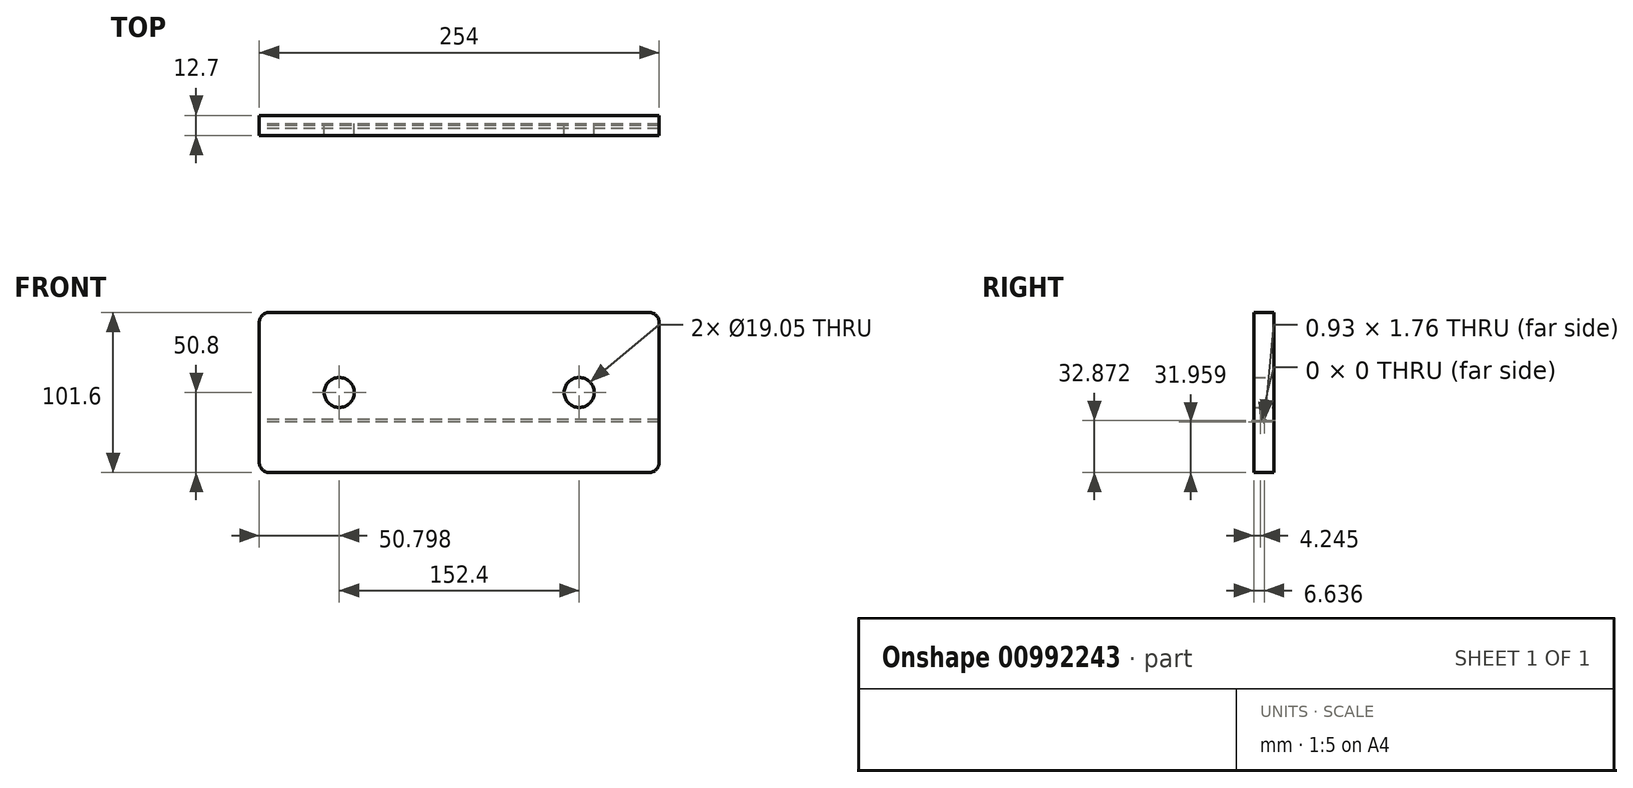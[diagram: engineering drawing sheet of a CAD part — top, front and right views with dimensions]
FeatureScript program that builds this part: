
annotation { "Feature Type Name" : "Feature", "Feature Type Description" : "" }
export const myFeature = defineFeature(function(context is Context, id is Id, definition is map)
    precondition{}
    {
        {
            var Q0;
            Q0=qCreatedBy(makeId("Front.planeOp"),FACE);
            var sketch = newSketch(context, id + "F0", { "sketchPlane" : qUnion([Q0])});
            skLineSegment(sketch, "E0.bottom", {"start": v(16.29, 17.05) * mm, "end": v(270.29, 17.05) * mm});
            skLineSegment(sketch, "E0.top", {"start": v(16.29, 118.65) * mm, "end": v(270.29, 118.65) * mm});
            skLineSegment(sketch, "E0.left", {"start": v(16.29, 17.05) * mm, "end": v(16.29, 118.65) * mm});
            skLineSegment(sketch, "E0.right", {"start": v(270.29, 17.05) * mm, "end": v(270.29, 118.65) * mm});
            skPoint(sketch, "E1", {"position": v(67.09, 67.85) * mm});
            skPoint(sketch, "E2", {"position": v(219.49, 67.85) * mm});
            skCircle(sketch, "E3", {"center": v(67.09, 67.85) * mm, "radius": 9.53 * mm});
            skCircle(sketch, "E4", {"center": v(219.49, 67.85) * mm, "radius": 9.53 * mm});
            skPoint(sketch, "E5.start.orphan", {"position": v(16.29, 67.85) * mm});
            skPoint(sketch, "E6.trimOffspring.end.orphan", {"position": v(270.29, 67.85) * mm});
            skSolve(sketch);
        }
        {
            var Q0;
            Q0 = qSketchRegion(id + "F0", true);
            extrude(context, id + "F1", {"entities" : qUnion([Q0]), "depth" : 12.7 * mm, "offsetDistance" : 25.4 * mm});
        }
        {
            var Q0;
            Q0=makeQuery(id+"F1.opExtrude","SWEPT_EDGE",EDGE,{"disambiguationData":[OSD([sQuery(id+"F0.wireOp",EDGE,"E0.top"),sQuery(id+"F0.wireOp",EDGE,"E0.left")])]});
            var Q1;
            Q1=makeQuery(id+"F1.opExtrude","SWEPT_EDGE",EDGE,{"disambiguationData":[OSD([sQuery(id+"F0.wireOp",EDGE,"E0.bottom"),sQuery(id+"F0.wireOp",EDGE,"E0.left")])]});
            var Q2;
            Q2=makeQuery(id+"F1.opExtrude","SWEPT_EDGE",EDGE,{"disambiguationData":[OSD([sQuery(id+"F0.wireOp",EDGE,"E0.top"),sQuery(id+"F0.wireOp",EDGE,"E0.right")])]});
            var Q3;
            Q3=makeQuery(id+"F1.opExtrude","SWEPT_EDGE",EDGE,{"disambiguationData":[OSD([sQuery(id+"F0.wireOp",EDGE,"E0.bottom"),sQuery(id+"F0.wireOp",EDGE,"E0.right")])]});
            fillet(context, id + "F2", {"entities" : qUnion([Q0, Q1, Q2, Q3]), "radius" : 6.35 * mm, "tangentPropagation" : true, "allowEdgeOverflow" : false});
        }
        {
            var Q0;
            Q0 = qSketchRegion(id + "F0", true);
            extrude(context, id + "F3", {"entities" : qUnion([Q0]), "operationType" : NewBodyOperationType.ADD, "depth" : 12.7 * mm, "offsetDistance" : 25.4 * mm});
        }
        {
            var Q0;
            Q0=makeQuery(id+"F3.opExtrude","SWEPT_EDGE",EDGE,{"disambiguationData":[OSD([sQuery(id+"F0.wireOp",EDGE,"E0.top"),sQuery(id+"F0.wireOp",EDGE,"E0.right")])]});
            var Q1;
            Q1=makeQuery(id+"F3.opExtrude","SWEPT_EDGE",EDGE,{"disambiguationData":[OSD([sQuery(id+"F0.wireOp",EDGE,"E0.top"),sQuery(id+"F0.wireOp",EDGE,"E0.left")])]});
            var Q2;
            Q2=makeQuery(id+"F3.opExtrude","SWEPT_EDGE",EDGE,{"disambiguationData":[OSD([sQuery(id+"F0.wireOp",EDGE,"E0.bottom"),sQuery(id+"F0.wireOp",EDGE,"E0.right")])]});
            var Q3;
            Q3=makeQuery(id+"F3.opExtrude","SWEPT_EDGE",EDGE,{"disambiguationData":[OSD([sQuery(id+"F0.wireOp",EDGE,"E0.bottom"),sQuery(id+"F0.wireOp",EDGE,"E0.left")])]});
            fillet(context, id + "F4", {"entities" : qUnion([Q0, Q1, Q2, Q3]), "radius" : 6.35 * mm, "tangentPropagation" : true, "allowEdgeOverflow" : false});
        }
        {
            var Q0;
            {var subQ0=sQuery(id+"F0.wireOp",EDGE,"E0.left");Q0=makeQuery(id+"F3.boolean.opBoolean","MERGE",FACE,{"derivedFrom":[makeQuery(id+"F1.opExtrude","SWEPT_FACE",FACE,{"disambiguationData":[OSD([subQ0])]}),makeQuery(id+"F3.opExtrude","SWEPT_FACE",FACE,{"disambiguationData":[OSD([subQ0])]})]});}
            var sketch = newSketch(context, id + "F5", { "sketchPlane" : qUnion([Q0])});
            skLineSegment(sketch, "E7.bottom", {"start": v(5.6, 50.8) * mm, "end": v(6.53, 50.8) * mm});
            skLineSegment(sketch, "E7.top", {"start": v(5.6, 49.04) * mm, "end": v(6.53, 49.04) * mm});
            skLineSegment(sketch, "E7.left", {"start": v(5.6, 49.04) * mm, "end": v(5.6, 50.8) * mm});
            skLineSegment(sketch, "E7.right", {"start": v(6.53, 49.04) * mm, "end": v(6.53, 50.8) * mm});
            skLineSegment(sketch, "E8.bottom", {"start": v(8.45, 49) * mm, "end": v(8.46, 49) * mm});
            skLineSegment(sketch, "E8.top", {"start": v(8.45, 49) * mm, "end": v(8.46, 49) * mm});
            skLineSegment(sketch, "E8.left", {"start": v(8.45, 49) * mm, "end": v(8.45, 49) * mm});
            skLineSegment(sketch, "E8.right", {"start": v(8.46, 49) * mm, "end": v(8.46, 49) * mm});
            skSolve(sketch);
        }
        {
            var Q0;
            Q0=makeQuery(id+"F5.imprint","IMPRINT",FACE,{"disambiguationData":[TD([[makeQuery(id+"F5.imprint","IMPRINT",EDGE,{"derivedFrom":sQuery(id+"F5.wireOp",EDGE,"E7.bottom")}),-1.0]])]});
            extrude(context, id + "F6", {"entities" : qUnion([Q0]), "operationType" : NewBodyOperationType.REMOVE, "endBound" : BoundingType.THROUGH_ALL, "oppositeDirection" : true, "depth" : 268.22 * mm, "offsetDistance" : 25.4 * mm});
        }
        {
            var Q0;
            Q0=makeQuery(id+"F5.imprint","IMPRINT",FACE,{"disambiguationData":[TD([[makeQuery(id+"F5.imprint","IMPRINT",EDGE,{"derivedFrom":sQuery(id+"F5.wireOp",EDGE,"E8.bottom")}),-1.0]])]});
            extrude(context, id + "F7", {"entities" : qUnion([Q0]), "operationType" : NewBodyOperationType.REMOVE, "endBound" : BoundingType.THROUGH_ALL, "oppositeDirection" : true, "depth" : 25.4 * mm, "offsetDistance" : 25.4 * mm});
        }
    });
